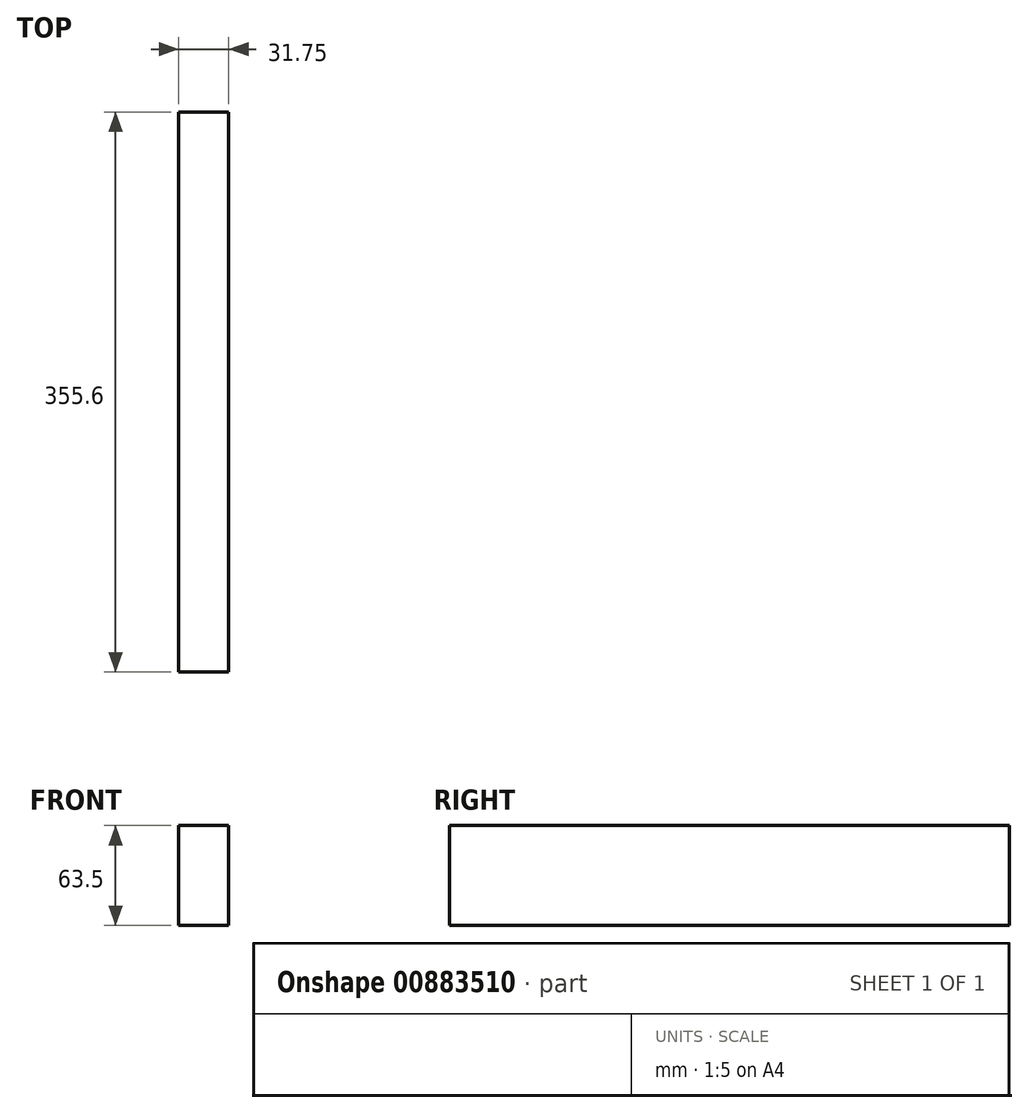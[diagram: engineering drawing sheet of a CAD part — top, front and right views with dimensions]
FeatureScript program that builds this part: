
annotation { "Feature Type Name" : "Feature", "Feature Type Description" : "" }
export const myFeature = defineFeature(function(context is Context, id is Id, definition is map)
    precondition{}
    {
        {
            var Q0;
            Q0=qCreatedBy(makeId("Front.planeOp"),FACE);
            var sketch = newSketch(context, id + "F0", { "sketchPlane" : qUnion([Q0])});
            skLineSegment(sketch, "E0.bottom", {"start": v(0, 0) * mm, "end": v(31.75, 0) * mm});
            skLineSegment(sketch, "E0.top", {"start": v(0, 63.5) * mm, "end": v(31.75, 63.5) * mm});
            skLineSegment(sketch, "E0.left", {"start": v(0, 0) * mm, "end": v(0, 63.5) * mm});
            skLineSegment(sketch, "E0.right", {"start": v(31.75, 0) * mm, "end": v(31.75, 63.5) * mm});
            skSolve(sketch);
        }
        {
            var Q0;
            Q0=qSketchRegion(id+"F0",true);
            extrude(context, id + "F1", {"entities" : qUnion([Q0]), "depth" : 355.6 * mm, "offsetDistance" : 25.4 * mm});
        }
    });
